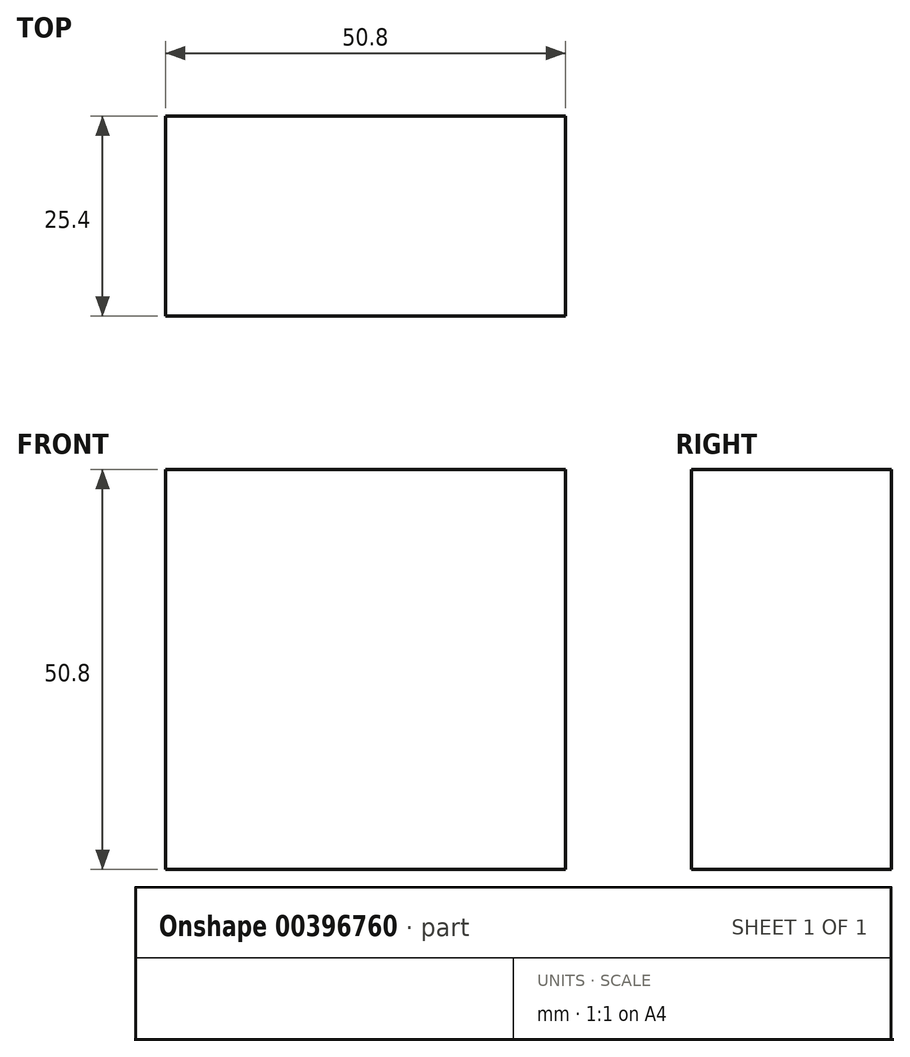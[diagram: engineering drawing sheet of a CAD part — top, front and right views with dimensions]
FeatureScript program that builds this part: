
annotation { "Feature Type Name" : "Feature", "Feature Type Description" : "" }
export const myFeature = defineFeature(function(context is Context, id is Id, definition is map)
    precondition{}
    {
        {
            var Q0;
            Q0=qCreatedBy(makeId("Front.planeOp"),FACE);
            var sketch = newSketch(context, id + "F0", { "sketchPlane" : qUnion([Q0])});
            skLineSegment(sketch, "E0.bottom", {"start": v(0, 0) * mm, "end": v(-50.8, 0) * mm});
            skLineSegment(sketch, "E0.top", {"start": v(0, 50.8) * mm, "end": v(-50.8, 50.8) * mm});
            skLineSegment(sketch, "E0.left", {"start": v(0, 0) * mm, "end": v(0, 50.8) * mm});
            skLineSegment(sketch, "E0.right", {"start": v(-50.8, 0) * mm, "end": v(-50.8, 50.8) * mm});
            skSolve(sketch);
        }
        {
            var Q0;
            Q0 = qSketchRegion(id + "F0", true);
            extrude(context, id + "F1", {"entities" : qUnion([Q0]), "depth" : 25.4 * mm});
        }
    });
